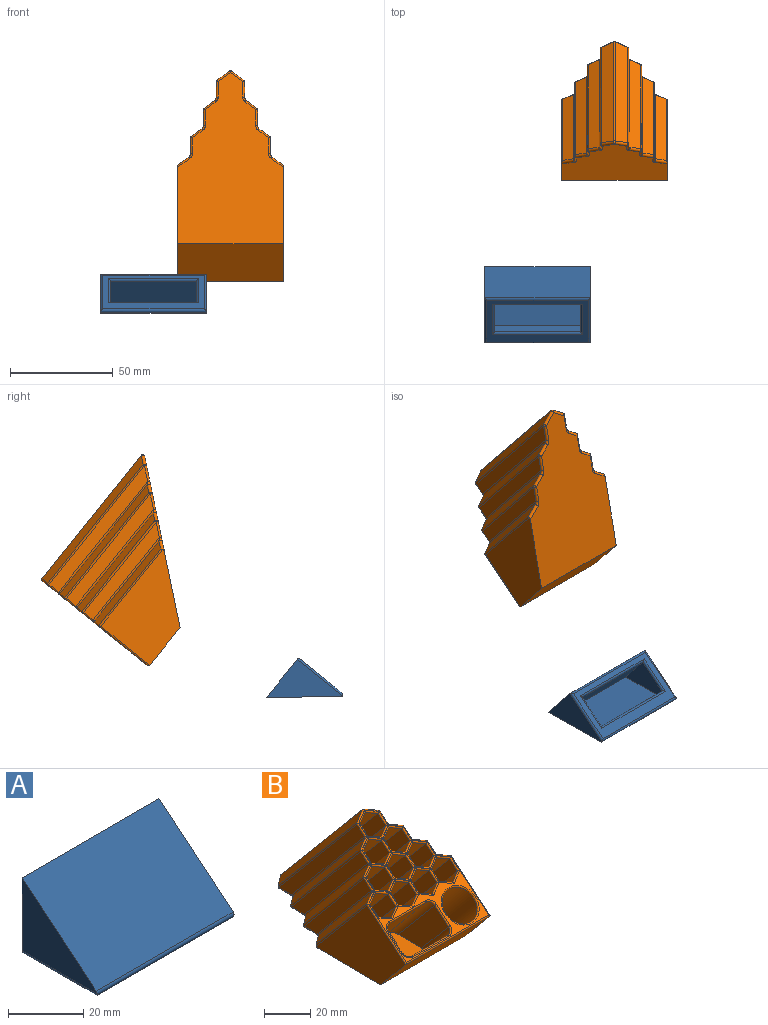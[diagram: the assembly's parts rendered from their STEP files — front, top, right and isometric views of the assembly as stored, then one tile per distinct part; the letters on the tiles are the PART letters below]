
ASSEMBLY  parts=2 mates=4
PART A: 18 faces, bbox 51.5x28.2x24.7 mm
  f0: plane 51.5x27.88mm, normal (0,-0.64,0.77), area 1858.8mm2, adj f2,f3,f4,f17
  f1: plane 49.5x26.24mm, normal (0,0,-1), area 463mm2, adj f10,f11,f12,f13,f14,f15,f16,f17
  f2: plane 51.5x23.7mm, normal (0,1,0), area 1220.4mm2, adj f0,f3,f4,f14
  f3: plane 28.24x23.7mm, normal (1,0,0), area 341.3mm2, adj f0,f2,f15,f17
  f4: plane 28.24x23.7mm, normal (-1,0,0), area 341.3mm2, adj f0,f2,f16,f17
  f5: plane 42x17mm, normal (0,0.64,-0.77), area 924.4mm2, adj f6,f7,f8,f9
  f6: plane 42x4.99mm, normal (0,1,0), area 209.6mm2, adj f5,f7,f8,f11
  f7: plane 18.97x17mm, normal (-1,0,0), area 203.7mm2, adj f5,f6,f9,f10
  f8: plane 18.97x17mm, normal (1,0,0), area 203.7mm2, adj f5,f6,f9,f13
  f9: plane 42x18.97mm, normal (0,-1,0), area 796.7mm2, adj f5,f7,f8,f12
  f10: cylinder r=1mm len=19mm, axis (0,-1,0), area 27.8mm2, adj f1,f7,f11,f12
  f11: cylinder r=1mm len=44mm, axis (-1,0,0), area 67.1mm2, adj f1,f6,f10,f13
  f12: cylinder r=1mm len=44mm, axis (1,0,0), area 67.1mm2, adj f1,f9,f10,f13
  f13: cylinder r=1mm len=19mm, axis (0,1,0), area 27.8mm2, adj f1,f8,f11,f12
  f14: cylinder r=1mm len=51.5mm, axis (-1,0,0), area 79.8mm2, adj f1,f2,f15,f16
  f15: cylinder r=1mm len=28.24mm, axis (0,-1,0), area 43.2mm2, adj f1,f3,f14,f17
  f16: cylinder r=1mm len=28.24mm, axis (0,1,0), area 43.2mm2, adj f1,f4,f14,f17
  f17: cylinder r=1mm len=51.5mm, axis (-1,0,0), area 125.2mm2, adj f0,f1,f3,f4,f15,f16
PART B: 242 faces, bbox 52.7x101.9x70.6 mm
  f0: plane 31.69x29mm, normal (-0.5,0.66,0.56), area 253mm2, adj f5,f11,f36,f100,f101,f168
  f1: plane 31.69x29mm, normal (0.5,0.66,0.56), area 253mm2, adj f6,f10,f43,f102,f103,f170
  f2: plane 31.69x29mm, normal (-0.5,0.66,0.56), area 253mm2, adj f7,f9,f54,f104,f105,f181
  f3: plane 31.69x29mm, normal (0.5,0.66,0.56), area 253mm2, adj f4,f8,f65,f106,f107,f192
  f4: plane 31.69x29mm, normal (-0.5,0.66,0.56), area 253mm2, adj f3,f8,f86,f106,f107,f190
  f5: plane 31.69x29mm, normal (0.5,0.66,0.56), area 253mm2, adj f0,f11,f39,f100,f101,f169
  f6: plane 31.69x29mm, normal (-0.5,0.66,0.56), area 253mm2, adj f1,f10,f40,f102,f103,f171
  f7: plane 31.69x29mm, normal (0.5,0.66,0.56), area 253mm2, adj f2,f9,f57,f104,f105,f179
  f8: plane 15.34x11mm, normal (0,-0.01,1), area 134mm2, adj f3,f4,f63,f64,f65,f86,f106
  f9: plane 15.34x11mm, normal (0,-0.01,1), area 134mm2, adj f2,f7,f54,f55,f56,f57,f104
  f10: plane 15.34x11mm, normal (0,-0.01,1), area 134mm2, adj f1,f6,f40,f41,f42,f43,f102
  f11: plane 15.34x11mm, normal (0,-0.01,1), area 134mm2, adj f0,f5,f36,f37,f38,f39,f100
  f12: cylinder r=3mm len=30.05mm, axis (0,-0.64,0.77), area 168.8mm2, adj f13,f19,f99,f129
  f13: plane 30.44x26.37mm, normal (1,0,0), area 326.9mm2, adj f12,f14,f99,f127
  f14: cylinder r=3mm len=21.23mm, axis (0,-0.64,0.77), area 111.3mm2, adj f13,f15,f99,f126
  f15: plane 22x17.41mm, normal (0,0.77,0.64), area 500.1mm2, adj f14,f16,f99,f128
  f16: cylinder r=3mm len=21.23mm, axis (0,-0.64,0.77), area 111.3mm2, adj f15,f17,f99,f130
  f17: plane 30.44x26.37mm, normal (-1,0,0), area 326.9mm2, adj f16,f18,f99,f132
  f18: cylinder r=3mm len=30.05mm, axis (0,-0.64,0.77), area 168.8mm2, adj f17,f19,f99,f133
  f19: plane 28.12x23.6mm, normal (0,-0.77,-0.64), area 807.6mm2, adj f12,f18,f99,f131
  f20: cylinder r=8.5mm len=39.12mm, axis (0,-0.64,0.77), area 1587.3mm2, adj f98,f108
  f21: plane 52.16x46.17mm, normal (0.5,0.66,0.56), area 423.8mm2, adj f22,f88,f96,f135
  f22: plane 52.16x46.17mm, normal (-0.5,0.66,0.56), area 423.8mm2, adj f21,f23,f96,f137
  f23: plane 56.21x51.96mm, normal (-1,0,0), area 448.7mm2, adj f22,f24,f96,f139
  f24: plane 58.17x51.2mm, normal (-0.5,-0.66,-0.56), area 473.6mm2, adj f23,f25,f96,f138
  f25: plane 58.17x51.2mm, normal (0.5,-0.66,-0.56), area 473.6mm2, adj f24,f88,f96,f136
  f26: plane 49.39x46.24mm, normal (1,0,0), area 392.2mm2, adj f27,f81,f95,f151
  f27: plane 45.34x40.45mm, normal (0.5,0.66,0.56), area 367.3mm2, adj f26,f28,f95,f150
  f28: plane 45.34x40.45mm, normal (-0.5,0.66,0.56), area 367.3mm2, adj f27,f29,f95,f148
  f29: plane 49.39x46.24mm, normal (-1,0,0), area 392.2mm2, adj f28,f30,f95,f146
  f30: plane 51.35x45.48mm, normal (-0.5,-0.66,-0.56), area 417mm2, adj f29,f81,f95,f147
  f31: plane 38.53x34.72mm, normal (-0.5,0.66,0.56), area 310.8mm2, adj f32,f82,f93,f162
  f32: plane 42.57x40.51mm, normal (-1,0,0), area 335.6mm2, adj f31,f33,f93,f163
  f33: plane 44.53x39.76mm, normal (-0.5,-0.66,-0.56), area 360.5mm2, adj f32,f34,f93,f161
  f34: plane 44.53x39.76mm, normal (0.5,-0.66,-0.56), area 360.5mm2, adj f33,f35,f93,f159
  f35: plane 42.57x40.51mm, normal (1,0,0), area 335.6mm2, adj f34,f82,f93,f158
  f36: plane 35.75x34.79mm, normal (-1,0,0), area 279.1mm2, adj f0,f11,f37,f166
  f37: plane 37.71x34.04mm, normal (-0.5,-0.66,-0.56), area 304mm2, adj f11,f36,f38,f164
  f38: plane 37.71x34.04mm, normal (0.5,-0.66,-0.56), area 304mm2, adj f11,f37,f39,f165
  f39: plane 35.75x34.79mm, normal (1,0,0), area 279.1mm2, adj f5,f11,f38,f167
  f40: plane 35.75x34.79mm, normal (-1,0,0), area 279.1mm2, adj f6,f10,f41,f173
  f41: plane 37.71x34.04mm, normal (-0.5,-0.66,-0.56), area 304mm2, adj f10,f40,f42,f175
  f42: plane 37.71x34.04mm, normal (0.5,-0.66,-0.56), area 304mm2, adj f10,f41,f43,f174
  f43: plane 35.75x34.79mm, normal (1,0,0), area 279.1mm2, adj f1,f10,f42,f172
  f44: plane 42.57x40.51mm, normal (-1,0,0), area 335.6mm2, adj f45,f83,f92,f153
  f45: plane 44.53x39.76mm, normal (-0.5,-0.66,-0.56), area 360.5mm2, adj f44,f46,f92,f155
  f46: plane 44.53x39.76mm, normal (0.5,-0.66,-0.56), area 360.5mm2, adj f45,f47,f92,f157
  f47: plane 42.57x40.51mm, normal (1,0,0), area 335.6mm2, adj f46,f48,f92,f156
  f48: plane 38.53x34.72mm, normal (0.5,0.66,0.56), area 310.8mm2, adj f47,f83,f92,f154
  f49: plane 45.34x40.45mm, normal (-0.5,0.66,0.56), area 367.3mm2, adj f50,f84,f94,f140
  f50: plane 49.39x46.24mm, normal (-1,0,0), area 392.2mm2, adj f49,f51,f94,f141
  f51: plane 51.35x45.48mm, normal (-0.5,-0.66,-0.56), area 417mm2, adj f50,f52,f94,f143
  f52: plane 51.35x45.48mm, normal (0.5,-0.66,-0.56), area 417mm2, adj f51,f53,f94,f145
  f53: plane 49.39x46.24mm, normal (1,0,0), area 392.2mm2, adj f52,f84,f94,f144
  f54: plane 35.75x34.79mm, normal (-1,0,0), area 279.1mm2, adj f2,f9,f55,f180
  f55: plane 37.71x34.04mm, normal (-0.5,-0.66,-0.56), area 304mm2, adj f9,f54,f56,f178
  f56: plane 37.71x34.04mm, normal (0.5,-0.66,-0.56), area 304mm2, adj f9,f55,f57,f176
  f57: plane 35.75x34.79mm, normal (1,0,0), area 279.1mm2, adj f7,f9,f56,f177
  f58: plane 38.53x34.72mm, normal (-0.5,0.66,0.56), area 310.8mm2, adj f59,f85,f91,f185
  f59: plane 42.57x40.51mm, normal (-1,0,0), area 335.6mm2, adj f58,f60,f91,f183
  f60: plane 44.53x39.76mm, normal (-0.5,-0.66,-0.56), area 360.5mm2, adj f59,f61,f91,f182
  f61: plane 44.53x39.76mm, normal (0.5,-0.66,-0.56), area 360.5mm2, adj f60,f62,f91,f184
  f62: plane 42.57x40.51mm, normal (1,0,0), area 335.6mm2, adj f61,f85,f91,f186
  f63: plane 37.71x34.04mm, normal (-0.5,-0.66,-0.56), area 304mm2, adj f8,f64,f86,f189
  f64: plane 37.71x34.04mm, normal (0.5,-0.66,-0.56), area 304mm2, adj f8,f63,f65,f191
  f65: plane 35.75x34.79mm, normal (1,0,0), area 279.1mm2, adj f3,f8,f64,f193
  f66: plane 43.29x40.9mm, normal (1,0,0), area 326.8mm2, adj f120,f235,f238,f241
  f67: plane 38.34x34.46mm, normal (0.5,0.66,0.56), area 295.5mm2, adj f122,f233,f237,f238
  f68: plane 54.31x37.77mm, normal (1,0,0), area 1106.6mm2, adj f90,f97,f124,f233,f237
  f69: plane 54.31x37.77mm, normal (-1,0,0), area 1106.6mm2, adj f90,f97,f123,f195,f197
  f70: plane 38.34x34.46mm, normal (-0.5,0.66,0.56), area 295.5mm2, adj f121,f195,f196,f197
  f71: plane 43.29x40.9mm, normal (-1,0,0), area 326.8mm2, adj f119,f196,f199,f200
  f72: plane 45.16x40.18mm, normal (-0.5,0.66,0.56), area 349.5mm2, adj f117,f199,f203,f204
  f73: plane 50.1x46.62mm, normal (-1,0,0), area 380.8mm2, adj f115,f203,f206,f207
  f74: plane 51.98x45.9mm, normal (-0.5,0.66,0.56), area 403.4mm2, adj f113,f206,f210,f211
  f75: plane 56.92x52.34mm, normal (-1,0,0), area 434.7mm2, adj f111,f210,f213,f214
  f76: plane 59.07x52.18mm, normal (-0.5,0.66,0.56), area 524mm2, adj f109,f213,f216,f217
  f77: plane 59.07x52.18mm, normal (0.5,0.66,0.56), area 524mm2, adj f110,f216,f219,f220
  f78: plane 56.92x52.34mm, normal (1,0,0), area 434.7mm2, adj f112,f219,f223,f224
  f79: plane 51.98x45.9mm, normal (0.5,0.66,0.56), area 403.4mm2, adj f114,f223,f226,f227
  f80: plane 50.1x46.62mm, normal (1,0,0), area 380.8mm2, adj f116,f226,f230,f231
  f81: plane 51.35x45.48mm, normal (0.5,-0.66,-0.56), area 417mm2, adj f26,f30,f95,f149
  f82: plane 38.53x34.72mm, normal (0.5,0.66,0.56), area 310.8mm2, adj f31,f35,f93,f160
  f83: plane 38.53x34.72mm, normal (-0.5,0.66,0.56), area 310.8mm2, adj f44,f48,f92,f152
  f84: plane 45.34x40.45mm, normal (0.5,0.66,0.56), area 367.3mm2, adj f49,f53,f94,f142
  f85: plane 38.53x34.72mm, normal (0.5,0.66,0.56), area 310.8mm2, adj f58,f62,f91,f187
  f86: plane 35.75x34.79mm, normal (-1,0,0), area 279.1mm2, adj f4,f8,f63,f188
  f87: plane 45.16x40.18mm, normal (0.5,0.66,0.56), area 349.5mm2, adj f118,f230,f235,f236
  f88: plane 56.21x51.96mm, normal (1,0,0), area 448.7mm2, adj f21,f25,f96,f134
  f89: plane 50.66x50.1mm, normal (0,-0.64,0.77), area 283mm2, adj f108,f109,f110,f111,f112,f113,f114,f115
  f90: plane 85.25x51.5mm, normal (0,0.01,-1), area 3140mm2, adj f68,f69,f97,f197,f198,f200,f204,f205
  f91: plane 16.44x11mm, normal (0,-0.01,1), area 135.7mm2, adj f58,f59,f60,f61,f62,f85
  f92: plane 16.44x11mm, normal (0,-0.01,1), area 135.7mm2, adj f44,f45,f46,f47,f48,f83
  f93: plane 16.44x11mm, normal (0,-0.01,1), area 135.7mm2, adj f31,f32,f33,f34,f35,f82
  f94: plane 16.44x11mm, normal (0,-0.01,1), area 135.7mm2, adj f49,f50,f51,f52,f53,f84
  f95: plane 16.44x11mm, normal (0,-0.01,1), area 135.7mm2, adj f26,f27,f28,f29,f30,f81
  f96: plane 16.44x11mm, normal (0,-0.01,1), area 135.7mm2, adj f21,f22,f23,f24,f25,f88
  f97: plane 51.5x18.14mm, normal (0,-0.77,-0.64), area 1219.3mm2, adj f68,f69,f90,f125
  f98: plane 22.01x17mm, normal (0,-0.01,1), area 293.9mm2, adj f20
  f99: plane 28x22.01mm, normal (0,-0.01,1), area 606.3mm2, adj f12,f13,f14,f15,f16,f17,f18,f19
  f100: plane 3.97x0.46mm, normal (0,1,0.01), area 1.6mm2, adj f0,f5,f11,f101
  f101: plane 3.97x1.48mm, normal (0,-0.01,1), area 2.9mm2, adj f0,f5,f100
  f102: plane 3.97x0.46mm, normal (0,1,0.01), area 1.6mm2, adj f1,f6,f10,f103
  f103: plane 3.97x1.48mm, normal (0,-0.01,1), area 2.9mm2, adj f1,f6,f102
  f104: plane 3.97x0.46mm, normal (0,1,0.01), area 1.6mm2, adj f2,f7,f9,f105
  f105: plane 3.97x1.48mm, normal (0,-0.01,1), area 2.9mm2, adj f2,f7,f104
  f106: plane 3.97x0.46mm, normal (0,1,0.01), area 1.6mm2, adj f3,f4,f8,f107
  f107: plane 3.97x1.48mm, normal (0,-0.01,1), area 2.9mm2, adj f3,f4,f106
  f108: torus R=9.2mm, axis (0,0.64,-0.77), area 60.5mm2, adj f20,f89
  f109: cylinder r=0.7mm len=7.22mm, axis (0.87,0.38,0.32), area 8.3mm2, adj f76,f89,f110,f111,f213,f216
  f110: cylinder r=0.7mm len=7.22mm, axis (0.87,-0.38,-0.32), area 8.3mm2, adj f77,f89,f109,f112,f216,f219
  f111: cylinder r=0.7mm len=6.23mm, axis (0,0.77,0.64), area 7.4mm2, adj f75,f89,f109,f208,f213
  f112: cylinder r=0.7mm len=6.23mm, axis (0,-0.77,-0.64), area 7.4mm2, adj f78,f89,f110,f219,f221
  f113: cylinder r=0.7mm len=6.88mm, axis (0.87,0.38,0.32), area 7.4mm2, adj f74,f89,f115,f206,f208
  f114: cylinder r=0.7mm len=6.88mm, axis (0.87,-0.38,-0.32), area 7.4mm2, adj f79,f89,f116,f221,f226
  f115: cylinder r=0.7mm len=6.23mm, axis (0,0.77,0.64), area 7.4mm2, adj f73,f89,f113,f201,f206
  f116: cylinder r=0.7mm len=6.23mm, axis (0,-0.77,-0.64), area 7.4mm2, adj f80,f89,f114,f226,f228
  f117: cylinder r=0.7mm len=6.88mm, axis (0.87,0.38,0.32), area 7.4mm2, adj f72,f89,f119,f199,f201
  f118: cylinder r=0.7mm len=6.88mm, axis (0.87,-0.38,-0.32), area 7.4mm2, adj f87,f89,f120,f228,f235
  f119: cylinder r=0.7mm len=6.23mm, axis (0,0.77,0.64), area 7.4mm2, adj f71,f89,f117,f194,f199
  f120: cylinder r=0.7mm len=6.23mm, axis (0,-0.77,-0.64), area 7.4mm2, adj f66,f89,f118,f234,f235
  f121: cylinder r=0.7mm len=6.88mm, axis (0.87,0.38,0.32), area 7.4mm2, adj f70,f89,f123,f194,f195
  f122: cylinder r=0.7mm len=6.88mm, axis (0.87,-0.38,-0.32), area 7.4mm2, adj f67,f89,f124,f233,f234
  f123: cylinder r=0.7mm len=24.23mm, axis (0,0.77,0.64), area 33.6mm2, adj f69,f89,f121,f125,f195
  f124: cylinder r=0.7mm len=24.23mm, axis (0,-0.77,-0.64), area 33.6mm2, adj f68,f89,f122,f125,f233
  f125: cylinder r=0.7mm len=51.5mm, axis (-1,0,0), area 56.1mm2, adj f89,f97,f123,f124
  f126: torus R=3.7mm, axis (0,0.64,-0.77), area 5.6mm2, adj f14,f89,f127,f128
  f127: cylinder r=0.7mm len=8.88mm, axis (0,-0.77,-0.64), area 12.1mm2, adj f13,f89,f126,f129
  f128: cylinder r=0.7mm len=22mm, axis (1,0,0), area 24.2mm2, adj f15,f89,f126,f130
  f129: torus R=3.7mm, axis (0,0.64,-0.77), area 5.6mm2, adj f12,f89,f127,f131
  f130: torus R=3.7mm, axis (0,0.64,-0.77), area 5.6mm2, adj f16,f89,f128,f132
  f131: cylinder r=0.7mm len=22mm, axis (-1,0,0), area 24.2mm2, adj f19,f89,f129,f133
  f132: cylinder r=0.7mm len=8.88mm, axis (0,0.77,0.64), area 12.1mm2, adj f17,f89,f130,f133
  f133: torus R=3.7mm, axis (0,0.64,-0.77), area 5.6mm2, adj f18,f89,f131,f132
  f134: cylinder r=0.7mm len=5.93mm, axis (0,-0.77,-0.64), area 7.3mm2, adj f88,f89,f135,f136
  f135: cylinder r=0.7mm len=6.55mm, axis (0.87,-0.38,-0.32), area 7.3mm2, adj f21,f89,f134,f137
  f136: cylinder r=0.7mm len=6.55mm, axis (-0.87,-0.38,-0.32), area 7.3mm2, adj f25,f89,f134,f138
  f137: cylinder r=0.7mm len=6.55mm, axis (0.87,0.38,0.32), area 7.3mm2, adj f22,f89,f135,f139
  f138: cylinder r=0.7mm len=6.55mm, axis (-0.87,0.38,0.32), area 7.3mm2, adj f24,f89,f136,f139
  f139: cylinder r=0.7mm len=5.93mm, axis (0,0.77,0.64), area 7.3mm2, adj f23,f89,f137,f138
  f140: cylinder r=0.7mm len=6.55mm, axis (0.87,0.38,0.32), area 7.3mm2, adj f49,f89,f141,f142
  f141: cylinder r=0.7mm len=5.93mm, axis (0,0.77,0.64), area 7.3mm2, adj f50,f89,f140,f143
  f142: cylinder r=0.7mm len=6.55mm, axis (0.87,-0.38,-0.32), area 7.3mm2, adj f84,f89,f140,f144
  f143: cylinder r=0.7mm len=6.55mm, axis (-0.87,0.38,0.32), area 7.3mm2, adj f51,f89,f141,f145
  f144: cylinder r=0.7mm len=5.93mm, axis (0,-0.77,-0.64), area 7.3mm2, adj f53,f89,f142,f145
  f145: cylinder r=0.7mm len=6.55mm, axis (-0.87,-0.38,-0.32), area 7.3mm2, adj f52,f89,f143,f144
  f146: cylinder r=0.7mm len=5.93mm, axis (0,0.77,0.64), area 7.3mm2, adj f29,f89,f147,f148
  f147: cylinder r=0.7mm len=6.55mm, axis (-0.87,0.38,0.32), area 7.3mm2, adj f30,f89,f146,f149
  f148: cylinder r=0.7mm len=6.55mm, axis (0.87,0.38,0.32), area 7.3mm2, adj f28,f89,f146,f150
  f149: cylinder r=0.7mm len=6.55mm, axis (-0.87,-0.38,-0.32), area 7.3mm2, adj f81,f89,f147,f151
  f150: cylinder r=0.7mm len=6.55mm, axis (0.87,-0.38,-0.32), area 7.3mm2, adj f27,f89,f148,f151
  f151: cylinder r=0.7mm len=5.93mm, axis (0,-0.77,-0.64), area 7.3mm2, adj f26,f89,f149,f150
  f152: cylinder r=0.7mm len=6.55mm, axis (0.87,0.38,0.32), area 7.3mm2, adj f83,f89,f153,f154
  f153: cylinder r=0.7mm len=5.93mm, axis (0,0.77,0.64), area 7.3mm2, adj f44,f89,f152,f155
  f154: cylinder r=0.7mm len=6.55mm, axis (0.87,-0.38,-0.32), area 7.3mm2, adj f48,f89,f152,f156
  f155: cylinder r=0.7mm len=6.55mm, axis (-0.87,0.38,0.32), area 7.3mm2, adj f45,f89,f153,f157
  f156: cylinder r=0.7mm len=5.93mm, axis (0,-0.77,-0.64), area 7.3mm2, adj f47,f89,f154,f157
  f157: cylinder r=0.7mm len=6.55mm, axis (-0.87,-0.38,-0.32), area 7.3mm2, adj f46,f89,f155,f156
  f158: cylinder r=0.7mm len=5.93mm, axis (0,-0.77,-0.64), area 7.3mm2, adj f35,f89,f159,f160
  f159: cylinder r=0.7mm len=6.55mm, axis (-0.87,-0.38,-0.32), area 7.3mm2, adj f34,f89,f158,f161
  f160: cylinder r=0.7mm len=6.55mm, axis (0.87,-0.38,-0.32), area 7.3mm2, adj f82,f89,f158,f162
  f161: cylinder r=0.7mm len=6.55mm, axis (-0.87,0.38,0.32), area 7.3mm2, adj f33,f89,f159,f163
  f162: cylinder r=0.7mm len=6.55mm, axis (0.87,0.38,0.32), area 7.3mm2, adj f31,f89,f160,f163
  f163: cylinder r=0.7mm len=5.93mm, axis (0,0.77,0.64), area 7.3mm2, adj f32,f89,f161,f162
  f164: cylinder r=0.7mm len=6.55mm, axis (-0.87,0.38,0.32), area 7.3mm2, adj f37,f89,f165,f166
  f165: cylinder r=0.7mm len=6.55mm, axis (-0.87,-0.38,-0.32), area 7.3mm2, adj f38,f89,f164,f167
  f166: cylinder r=0.7mm len=5.93mm, axis (0,0.77,0.64), area 7.3mm2, adj f36,f89,f164,f168
  f167: cylinder r=0.7mm len=5.93mm, axis (0,-0.77,-0.64), area 7.3mm2, adj f39,f89,f165,f169
  f168: cylinder r=0.7mm len=6.55mm, axis (0.87,0.38,0.32), area 7.3mm2, adj f0,f89,f166,f169
  f169: cylinder r=0.7mm len=6.55mm, axis (0.87,-0.38,-0.32), area 7.3mm2, adj f5,f89,f167,f168
  f170: cylinder r=0.7mm len=6.55mm, axis (0.87,-0.38,-0.32), area 7.3mm2, adj f1,f89,f171,f172
  f171: cylinder r=0.7mm len=6.55mm, axis (0.87,0.38,0.32), area 7.3mm2, adj f6,f89,f170,f173
  f172: cylinder r=0.7mm len=5.93mm, axis (0,-0.77,-0.64), area 7.3mm2, adj f43,f89,f170,f174
  f173: cylinder r=0.7mm len=5.93mm, axis (0,0.77,0.64), area 7.3mm2, adj f40,f89,f171,f175
  f174: cylinder r=0.7mm len=6.55mm, axis (-0.87,-0.38,-0.32), area 7.3mm2, adj f42,f89,f172,f175
  f175: cylinder r=0.7mm len=6.55mm, axis (-0.87,0.38,0.32), area 7.3mm2, adj f41,f89,f173,f174
  f176: cylinder r=0.7mm len=6.55mm, axis (-0.87,-0.38,-0.32), area 7.3mm2, adj f56,f89,f177,f178
  f177: cylinder r=0.7mm len=5.93mm, axis (0,-0.77,-0.64), area 7.3mm2, adj f57,f89,f176,f179
  f178: cylinder r=0.7mm len=6.55mm, axis (-0.87,0.38,0.32), area 7.3mm2, adj f55,f89,f176,f180
  f179: cylinder r=0.7mm len=6.55mm, axis (0.87,-0.38,-0.32), area 7.3mm2, adj f7,f89,f177,f181
  f180: cylinder r=0.7mm len=5.93mm, axis (0,0.77,0.64), area 7.3mm2, adj f54,f89,f178,f181
  f181: cylinder r=0.7mm len=6.55mm, axis (0.87,0.38,0.32), area 7.3mm2, adj f2,f89,f179,f180
  f182: cylinder r=0.7mm len=6.55mm, axis (-0.87,0.38,0.32), area 7.3mm2, adj f60,f89,f183,f184
  f183: cylinder r=0.7mm len=5.93mm, axis (0,0.77,0.64), area 7.3mm2, adj f59,f89,f182,f185
  f184: cylinder r=0.7mm len=6.55mm, axis (-0.87,-0.38,-0.32), area 7.3mm2, adj f61,f89,f182,f186
  f185: cylinder r=0.7mm len=6.55mm, axis (0.87,0.38,0.32), area 7.3mm2, adj f58,f89,f183,f187
  f186: cylinder r=0.7mm len=5.93mm, axis (0,-0.77,-0.64), area 7.3mm2, adj f62,f89,f184,f187
  f187: cylinder r=0.7mm len=6.55mm, axis (0.87,-0.38,-0.32), area 7.3mm2, adj f85,f89,f185,f186
  f188: cylinder r=0.7mm len=5.93mm, axis (0,0.77,0.64), area 7.3mm2, adj f86,f89,f189,f190
  f189: cylinder r=0.7mm len=6.55mm, axis (-0.87,0.38,0.32), area 7.3mm2, adj f63,f89,f188,f191
  f190: cylinder r=0.7mm len=6.55mm, axis (0.87,0.38,0.32), area 7.3mm2, adj f4,f89,f188,f192
  f191: cylinder r=0.7mm len=6.55mm, axis (-0.87,-0.38,-0.32), area 7.3mm2, adj f64,f89,f189,f193
  f192: cylinder r=0.7mm len=6.55mm, axis (0.87,-0.38,-0.32), area 7.3mm2, adj f3,f89,f190,f193
  f193: cylinder r=0.7mm len=5.93mm, axis (0,-0.77,-0.64), area 7.3mm2, adj f65,f89,f191,f192
  f194: bspline ~1.2x1.2mm, area 0.8mm2, adj f119,f121,f196
  f195: cylinder r=1mm len=37.7mm, axis (0,-0.64,0.77), area 50.3mm2, adj f69,f70,f121,f123,f197
  f196: cylinder r=1mm len=39.95mm, axis (0,0.64,-0.77), area 53mm2, adj f70,f71,f194,f198
  f197: cylinder r=1mm len=6.85mm, axis (-0.8,-0.6,-0.01), area 15.4mm2, adj f69,f70,f90,f195,f198
  f198: bspline ~2.89x2.16mm, area 3.5mm2, adj f90,f196,f197,f200
  f199: cylinder r=1mm len=44.08mm, axis (0,-0.64,0.77), area 59.3mm2, adj f71,f72,f117,f119,f202
  f200: cylinder r=1mm len=7.86mm, axis (0,-1,-0.01), area 12.3mm2, adj f71,f90,f198,f202
  f201: bspline ~1.2x1.2mm, area 0.8mm2, adj f115,f117,f203
  f202: sphere r=1mm, area 1.2mm2, adj f199,f200,f204
  f203: cylinder r=1mm len=46.76mm, axis (0,0.64,-0.77), area 62.3mm2, adj f72,f73,f201,f205
  f204: cylinder r=1mm len=5.85mm, axis (-0.8,-0.6,-0.01), area 14.1mm2, adj f72,f90,f202,f205
  f205: bspline ~2.89x2.16mm, area 3.5mm2, adj f90,f203,f204,f207
  f206: cylinder r=1mm len=50.9mm, axis (0,-0.64,0.77), area 68.6mm2, adj f73,f74,f113,f115,f209
  f207: cylinder r=1mm len=7.86mm, axis (0,-1,-0.01), area 12.3mm2, adj f73,f90,f205,f209
  f208: bspline ~1.25x1.2mm, area 0.8mm2, adj f111,f113,f210
  f209: sphere r=1mm, area 1.2mm2, adj f206,f207,f211
  f210: cylinder r=1mm len=53.58mm, axis (0,0.64,-0.77), area 71.7mm2, adj f74,f75,f208,f212
  f211: cylinder r=1mm len=5.85mm, axis (-0.8,-0.6,-0.01), area 14.1mm2, adj f74,f90,f209,f212
  f212: bspline ~2.24x1.59mm, area 3.5mm2, adj f90,f210,f211,f214
  f213: cylinder r=1mm len=57.72mm, axis (0,-0.64,0.77), area 77.9mm2, adj f75,f76,f109,f111,f215
  f214: cylinder r=1mm len=7.86mm, axis (0,-1,-0.01), area 12.3mm2, adj f75,f90,f212,f215
  f215: sphere r=1mm, area 1.2mm2, adj f213,f214,f217
  f216: cylinder r=1mm len=59.43mm, axis (0,-0.64,0.77), area 80.9mm2, adj f76,f77,f109,f110,f218
  f217: cylinder r=1mm len=6.6mm, axis (-0.8,-0.6,-0.01), area 16.1mm2, adj f76,f90,f215,f218
  f218: sphere r=1mm, area 2.1mm2, adj f216,f217,f220
  f219: cylinder r=1mm len=57.72mm, axis (0,-0.64,0.77), area 77.9mm2, adj f77,f78,f110,f112,f222
  f220: cylinder r=1mm len=6.6mm, axis (-0.8,0.6,0.01), area 16.1mm2, adj f77,f90,f218,f222
  f221: bspline ~1.2x1.2mm, area 0.8mm2, adj f112,f114,f223
  f222: sphere r=1mm, area 1.2mm2, adj f219,f220,f224
  f223: cylinder r=1mm len=53.58mm, axis (0,0.64,-0.77), area 71.7mm2, adj f78,f79,f221,f225
  f224: cylinder r=1mm len=7.86mm, axis (0,1,0.01), area 12.3mm2, adj f78,f90,f222,f225
  f225: bspline ~2.24x1.59mm, area 3.5mm2, adj f90,f223,f224,f227
  f226: cylinder r=1mm len=50.9mm, axis (0,-0.64,0.77), area 68.6mm2, adj f79,f80,f114,f116,f229
  f227: cylinder r=1mm len=5.85mm, axis (-0.8,0.6,0.01), area 14.1mm2, adj f79,f90,f225,f229
  f228: bspline ~1.25x1.2mm, area 0.8mm2, adj f116,f118,f230
  f229: sphere r=1mm, area 1.2mm2, adj f226,f227,f231
  f230: cylinder r=1mm len=46.76mm, axis (0,0.64,-0.77), area 62.3mm2, adj f80,f87,f228,f232
  f231: cylinder r=1mm len=7.86mm, axis (0,1,0.01), area 12.3mm2, adj f80,f90,f229,f232
  f232: bspline ~2.89x2.16mm, area 3.5mm2, adj f90,f230,f231,f236
  f233: cylinder r=1mm len=37.7mm, axis (0,-0.64,0.77), area 50.3mm2, adj f67,f68,f122,f124,f237
  f234: bspline ~1.25x1.2mm, area 0.8mm2, adj f120,f122,f238
  f235: cylinder r=1mm len=44.08mm, axis (0,-0.64,0.77), area 59.3mm2, adj f66,f87,f118,f120,f239
  f236: cylinder r=1mm len=5.85mm, axis (-0.8,0.6,0.01), area 14.1mm2, adj f87,f90,f232,f239
  f237: cylinder r=1mm len=6.85mm, axis (-0.8,0.6,0.01), area 15.4mm2, adj f67,f68,f90,f233,f240
  f238: cylinder r=1mm len=39.95mm, axis (0,0.64,-0.77), area 53mm2, adj f66,f67,f234,f240
  f239: sphere r=1mm, area 1.2mm2, adj f235,f236,f241
  f240: bspline ~2.89x2.16mm, area 3.5mm2, adj f90,f237,f238,f241
  f241: cylinder r=1mm len=7.86mm, axis (0,1,0.01), area 12.3mm2, adj f66,f90,f239,f240
PLACE A rot(axis=(0,-0.94,-0.33),180deg) t=(-31.48,-24.32,55.44)mm
PLACE B rot(axis=(0,-0.77,-0.64),180deg) t=(-38.48,-10.29,36.66)mm
MATE parallel A.f2 <-> B.f97  axis (0,0.78,0.63) through (-82.98,-23.31,24.54)mm
MATE parallel A.f2 <-> B.f97  axis (0,0.78,0.63) through (-82.98,-23.31,24.54)mm
MATE parallel A.f2 <-> B.f97  axis (0,0.78,0.63) through (-82.98,-23.31,24.54)mm
MATE parallel A.f2 <-> B.f97  axis (0,0.78,0.63) through (-82.98,-23.31,24.54)mm
